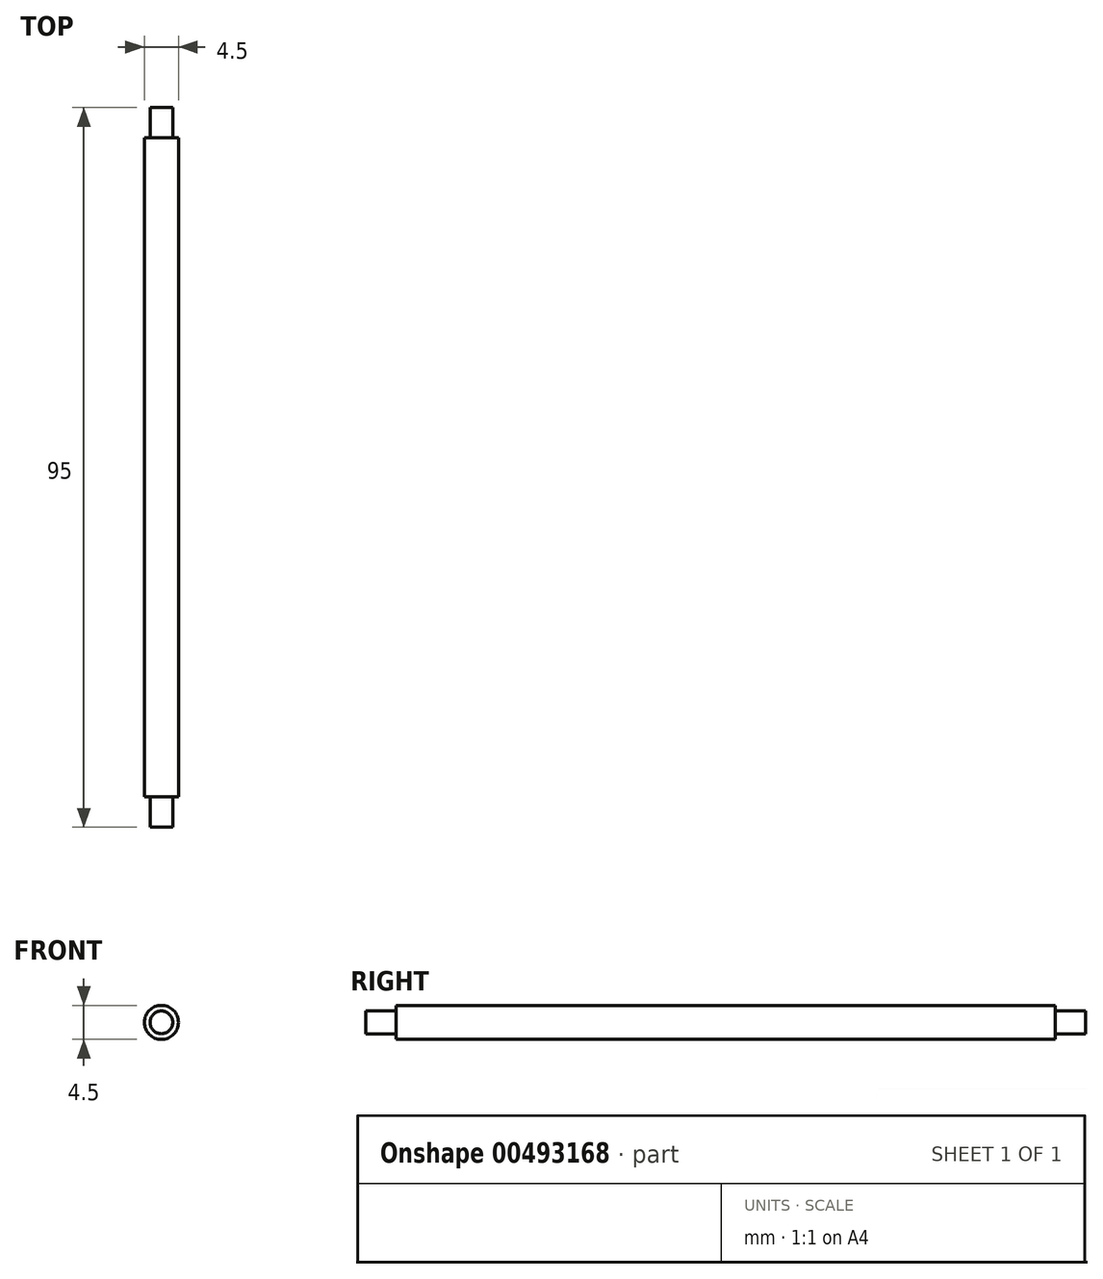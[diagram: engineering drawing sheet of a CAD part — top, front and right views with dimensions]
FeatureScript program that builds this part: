
annotation { "Feature Type Name" : "Feature", "Feature Type Description" : "" }
export const myFeature = defineFeature(function(context is Context, id is Id, definition is map)
    precondition{}
    {
        {
            var Q0;
            Q0=qCreatedBy(makeId("Front.planeOp"),FACE);
            var sketch = newSketch(context, id + "F0", { "sketchPlane" : qUnion([Q0])});
            skCircle(sketch, "E0", {"center": v(0, 0) * mm, "radius": 2.25 * mm});
            skSolve(sketch);
        }
        {
            var Q0;
            Q0=qSketchRegion(id+"F0",true);
            extrude(context, id + "F1", {"entities" : qUnion([Q0]), "depth" : 87 * mm});
        }
        {
            var Q0;
            Q0=makeQuery(id+"F1.opExtrude","CAP_FACE",FACE,{"disambiguationData":[OSD([sQuery(id+"F0.wireOp",EDGE,"E0")])],"isStart":true});
            var sketch = newSketch(context, id + "F2", { "sketchPlane" : qUnion([Q0])});
            skCircle(sketch, "E1", {"center": v(0, 0) * mm, "radius": 1.5 * mm});
            skSolve(sketch);
        }
        {
            var Q0;
            Q0 = qSketchRegion(id + "F2", true);
            extrude(context, id + "F3", {"entities" : qUnion([Q0]), "operationType" : NewBodyOperationType.ADD, "depth" : 4 * mm});
        }
        {
            var Q0;
            Q0=makeQuery(id+"F1.opExtrude","CAP_FACE",FACE,{"disambiguationData":[OSD([sQuery(id+"F0.wireOp",EDGE,"E0")])],"isStart":false});
            var sketch = newSketch(context, id + "F4", { "sketchPlane" : qUnion([Q0])});
            skCircle(sketch, "E2", {"center": v(0, 0) * mm, "radius": 1.5 * mm});
            skSolve(sketch);
        }
        {
            var Q0;
            Q0 = qSketchRegion(id + "F4", true);
            extrude(context, id + "F5", {"entities" : qUnion([Q0]), "operationType" : NewBodyOperationType.ADD, "depth" : 4 * mm});
        }
    });
